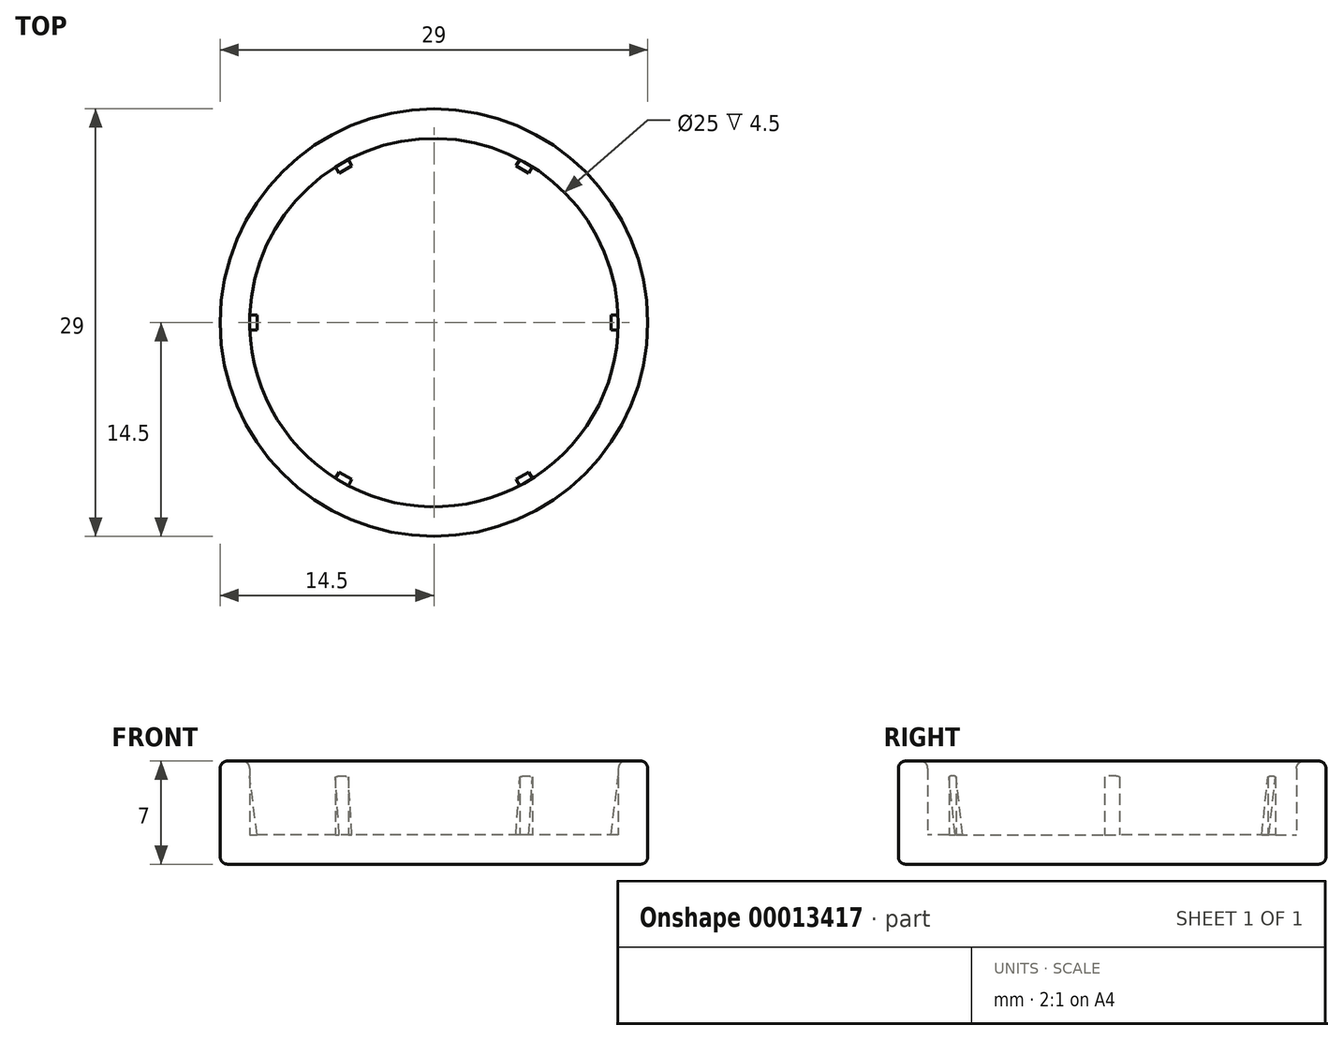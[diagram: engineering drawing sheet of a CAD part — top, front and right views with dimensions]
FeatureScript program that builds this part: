
annotation { "Feature Type Name" : "Feature", "Feature Type Description" : "" }
export const myFeature = defineFeature(function(context is Context, id is Id, definition is map)
    precondition{}
    {
        {
            var Q0;
            Q0=qCreatedBy(makeId("Front.planeOp"),FACE);
            var sketch = newSketch(context, id + "F0", { "sketchPlane" : qUnion([Q0])});
            skLineSegment(sketch, "E0.bottom", {"start": v(0, 0) * mm, "end": v(14.5, 0) * mm});
            skLineSegment(sketch, "E0.top", {"start": v(0, 2) * mm, "end": v(12.5, 2) * mm});
            skLineSegment(sketch, "E0.left", {"start": v(0, 0) * mm, "end": v(0, 2) * mm});
            skLineSegment(sketch, "E0.right", {"start": v(14.5, 0) * mm, "end": v(14.5, 2) * mm});
            skLineSegment(sketch, "E1.bottom", {"start": v(14.5, 0) * mm, "end": v(12.5, 0) * mm});
            skLineSegment(sketch, "E1.top", {"start": v(14.5, 7) * mm, "end": v(12.5, 7) * mm});
            skLineSegment(sketch, "E1.left", {"start": v(14.5, 0) * mm, "end": v(14.5, 7) * mm});
            skLineSegment(sketch, "E1.right", {"start": v(12.5, 2) * mm, "end": v(12.5, 7) * mm});
            skSolve(sketch);
        }
        {
            var Q0;
            Q0 = qSketchRegion(id + "F0", true);
            var Q1;
            Q1=sQuery(id+"F0.wireOp",EDGE,"E0.left");
            revolve(context, id + "F5", {"entities" : qUnion([Q0]), "axis" : qUnion([Q1]), "revolveType" : RevolveType.FULL});
        }
        {
            var Q0;
            Q0=makeQuery(id+"F5.opRevolve","SWEPT_FACE",FACE,{"disambiguationData":[OSD([sQuery(id+"F0.wireOp",EDGE,"E1.top")])]});
            fillet(context, id + "F1", {"entities" : qUnion([Q0]), "radius" : 0.5 * mm, "tangentPropagation" : true, "allowEdgeOverflow" : false});
        }
        {
            var Q0;
            Q0=makeQuery(id+"F5.opRevolve","SWEPT_FACE",FACE,{"disambiguationData":[OSD([sQuery(id+"F0.wireOp",EDGE,"E0.bottom"),sQuery(id+"F0.wireOp",EDGE,"E1.bottom")])]});
            fillet(context, id + "F6", {"entities" : qUnion([Q0]), "radius" : 0.5 * mm, "tangentPropagation" : true, "allowEdgeOverflow" : false});
        }
        {
            var Q0;
            Q0=qCreatedBy(makeId("Front.planeOp"),FACE);
            var sketch = newSketch(context, id + "F2", { "sketchPlane" : qUnion([Q0])});
            skLineSegment(sketch, "E2", {"start": v(12.5, 6) * mm, "end": v(12.5, 2) * mm});
            skLineSegment(sketch, "E3", {"start": v(12.5, 2) * mm, "end": v(12, 2) * mm});
            skLineSegment(sketch, "E4", {"start": v(12, 2) * mm, "end": v(12.5, 6) * mm});
            skSolve(sketch);
        }
        {
            var Q0;
            Q0 = qSketchRegion(id + "F2", true);
            extrude(context, id + "F3", {"entities" : qUnion([Q0]), "endBound" : BoundingType.SYMMETRIC, "depth" : 1 * mm});
        }
        {
            var Q0;
            Q0=makeQuery(id+"F3.opExtrude","SWEPT_BODY",BODY,{"disambiguationData":[OSD([sQuery(id+"F2.wireOp",EDGE,"E2"),sQuery(id+"F2.wireOp",EDGE,"E3"),sQuery(id+"F2.wireOp",EDGE,"E4")])]});
            var Q1;
            Q1=sQuery(id+"F0.wireOp",EDGE,"E0.left");
            circularPattern(context, id + "F4", {"operationType" : NewBodyOperationType.ADD, "entities" : qUnion([Q0]), "axis" : qUnion([Q1]), "angle" : 360 * degree, "instanceCount" : 6, "equalSpace" : true});
        }
    });
